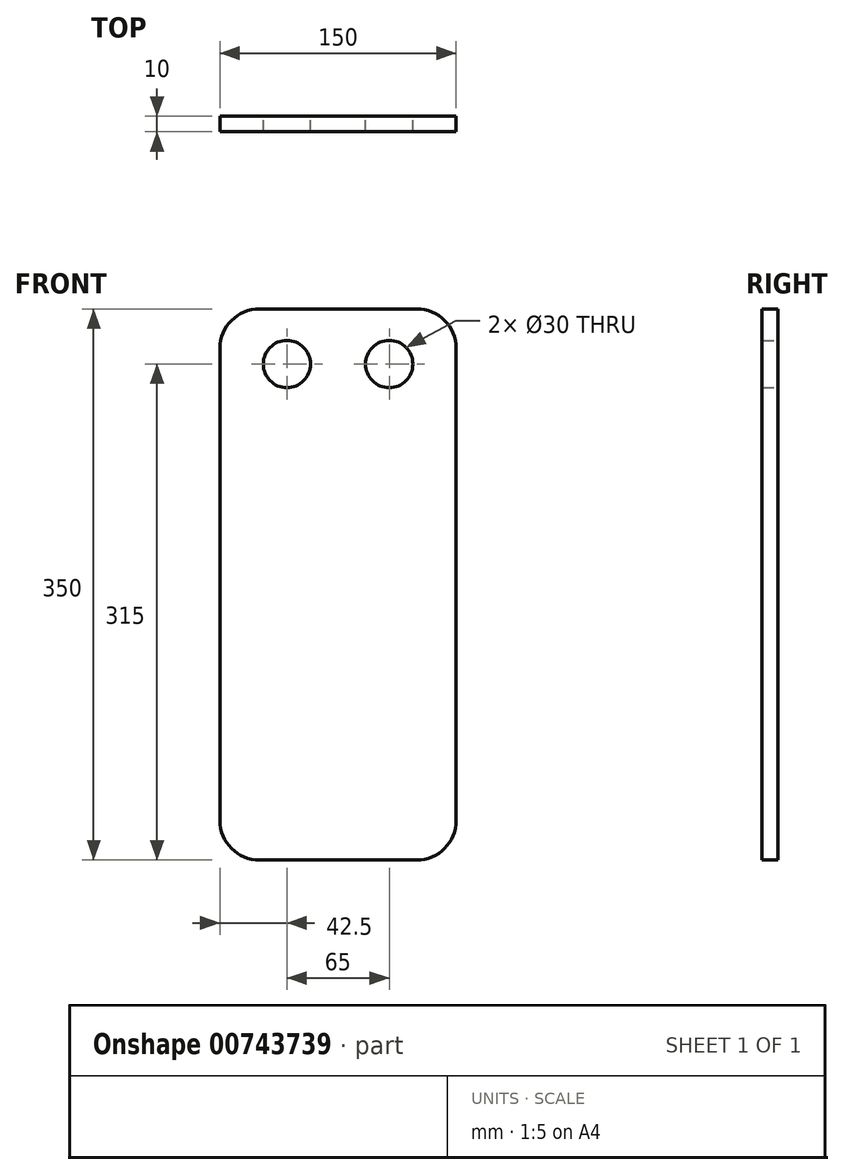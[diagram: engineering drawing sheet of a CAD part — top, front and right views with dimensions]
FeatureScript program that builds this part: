
annotation { "Feature Type Name" : "Feature", "Feature Type Description" : "" }
export const myFeature = defineFeature(function(context is Context, id is Id, definition is map)
    precondition{}
    {
        {
            var Q0;
            Q0=qCreatedBy(makeId("Front.planeOp"),FACE);
            var sketch = newSketch(context, id + "F0", { "sketchPlane" : qUnion([Q0])});
            skLineSegment(sketch, "E0.bottom", {"start": v(25, 0) * mm, "end": v(125, 0) * mm});
            skLineSegment(sketch, "E0.top", {"start": v(25, 350) * mm, "end": v(125, 350) * mm});
            skLineSegment(sketch, "E0.left", {"start": v(0, 25) * mm, "end": v(0, 325) * mm});
            skLineSegment(sketch, "E0.right", {"start": v(150, 25) * mm, "end": v(150, 325) * mm});
            skPoint(sketch, "E1.visualSharp", {"position": v(0, 350) * mm});
            skArc(sketch, "E1.filletArc", {"start": v(25, 350) * mm, "mid": v(7.32, 342.68) * mm, "end": v(0, 325) * mm});
            skPoint(sketch, "E2.visualSharp", {"position": v(150, 350) * mm});
            skArc(sketch, "E2.filletArc", {"start": v(150, 325) * mm, "mid": v(142.68, 342.68) * mm, "end": v(125, 350) * mm});
            skPoint(sketch, "E3.visualSharp", {"position": v(150, 0) * mm});
            skArc(sketch, "E3.filletArc", {"start": v(125, 0) * mm, "mid": v(142.68, 7.32) * mm, "end": v(150, 25) * mm});
            skPoint(sketch, "E4.visualSharp", {"position": v(0, 0) * mm});
            skArc(sketch, "E4.filletArc", {"start": v(0, 25) * mm, "mid": v(7.32, 7.32) * mm, "end": v(25, 0) * mm});
            skCircle(sketch, "E5", {"center": v(42.5, 315) * mm, "radius": 15 * mm});
            skCircle(sketch, "E6", {"center": v(107.5, 315) * mm, "radius": 15 * mm});
            skSolve(sketch);
        }
        {
            var Q0;
            Q0=makeQuery(id+"F0.imprint","IMPRINT",FACE,{"disambiguationData":[TD([[makeQuery(id+"F0.imprint","IMPRINT",EDGE,{"derivedFrom":sQuery(id+"F0.wireOp",EDGE,"E0.bottom")}),1.0]])]});
            extrude(context, id + "F1", {"entities" : qUnion([Q0]), "depth" : 10 * mm, "offsetDistance" : 25 * mm});
        }
    });
